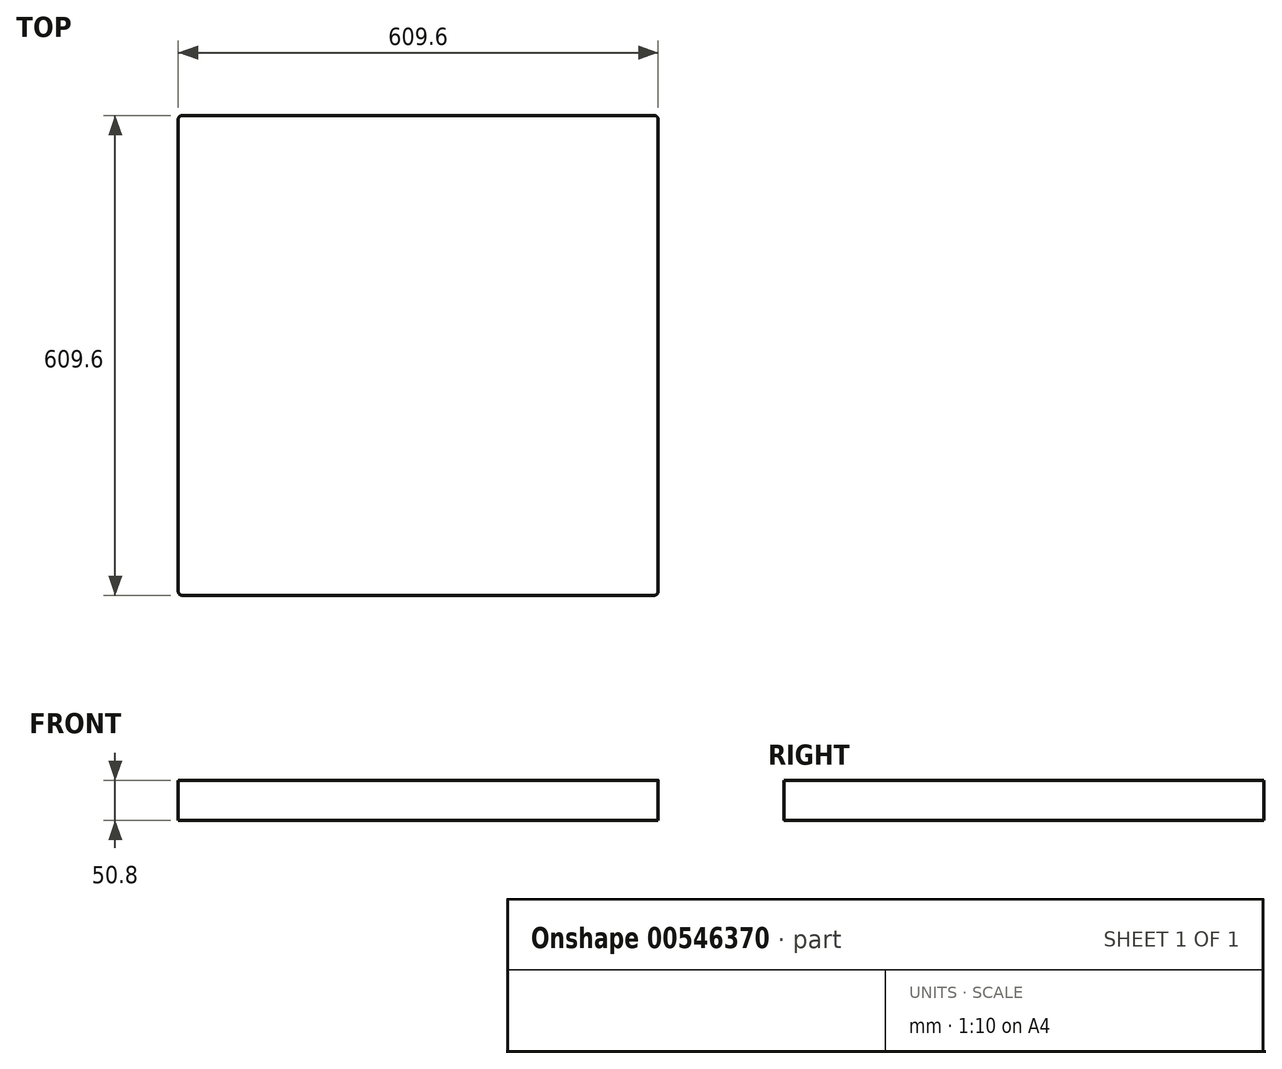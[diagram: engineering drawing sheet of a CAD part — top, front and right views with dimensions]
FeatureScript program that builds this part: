
annotation { "Feature Type Name" : "Feature", "Feature Type Description" : "" }
export const myFeature = defineFeature(function(context is Context, id is Id, definition is map)
    precondition{}
    {
        {
            var Q0;
            Q0=qCreatedBy(makeId("Front.planeOp"),FACE);
            var sketch = newSketch(context, id + "F0", { "sketchPlane" : qUnion([Q0])});
            skLineSegment(sketch, "E0.bottom", {"start": v(304.8, -25.4) * mm, "end": v(-304.8, -25.4) * mm});
            skLineSegment(sketch, "E0.top", {"start": v(304.8, 25.4) * mm, "end": v(-304.8, 25.4) * mm});
            skLineSegment(sketch, "E0.left", {"start": v(304.8, -25.4) * mm, "end": v(304.8, 25.4) * mm});
            skLineSegment(sketch, "E0.right", {"start": v(-304.8, -25.4) * mm, "end": v(-304.8, 25.4) * mm});
            skPoint(sketch, "E0.middle", {"position": v(0, 0) * mm});
            skSolve(sketch);
        }
        {
            var Q0;
            Q0=makeQuery(id+"F0.imprint","IMPRINT",FACE,{"disambiguationData":[TD([[makeQuery(id+"F0.imprint","IMPRINT",EDGE,{"derivedFrom":sQuery(id+"F0.wireOp",EDGE,"E0.bottom")}),-1.0]])]});
            extrude(context, id + "F1", {"entities" : qUnion([Q0]), "depth" : 609.6 * mm, "offsetDistance" : 25.4 * mm});
        }
        {
            var Q0;
            Q0=makeQuery(id+"F1.opExtrude","CAP_EDGE",EDGE,{"disambiguationData":[OSD([sQuery(id+"F0.wireOp",EDGE,"E0.left")])],"isStart":false});
            var Q1;
            Q1=makeQuery(id+"F1.opExtrude","CAP_EDGE",EDGE,{"disambiguationData":[OSD([sQuery(id+"F0.wireOp",EDGE,"E0.right")])],"isStart":true});
            var Q2;
            Q2=makeQuery(id+"F1.opExtrude","CAP_EDGE",EDGE,{"disambiguationData":[OSD([sQuery(id+"F0.wireOp",EDGE,"E0.right")])],"isStart":false});
            var Q3;
            Q3=makeQuery(id+"F1.opExtrude","CAP_EDGE",EDGE,{"disambiguationData":[OSD([sQuery(id+"F0.wireOp",EDGE,"E0.left")])],"isStart":true});
            fillet(context, id + "F2", {"entities" : qUnion([Q0, Q1, Q2, Q3]), "radius" : 5.08 * mm, "tangentPropagation" : true, "allowEdgeOverflow" : false});
        }
    });
